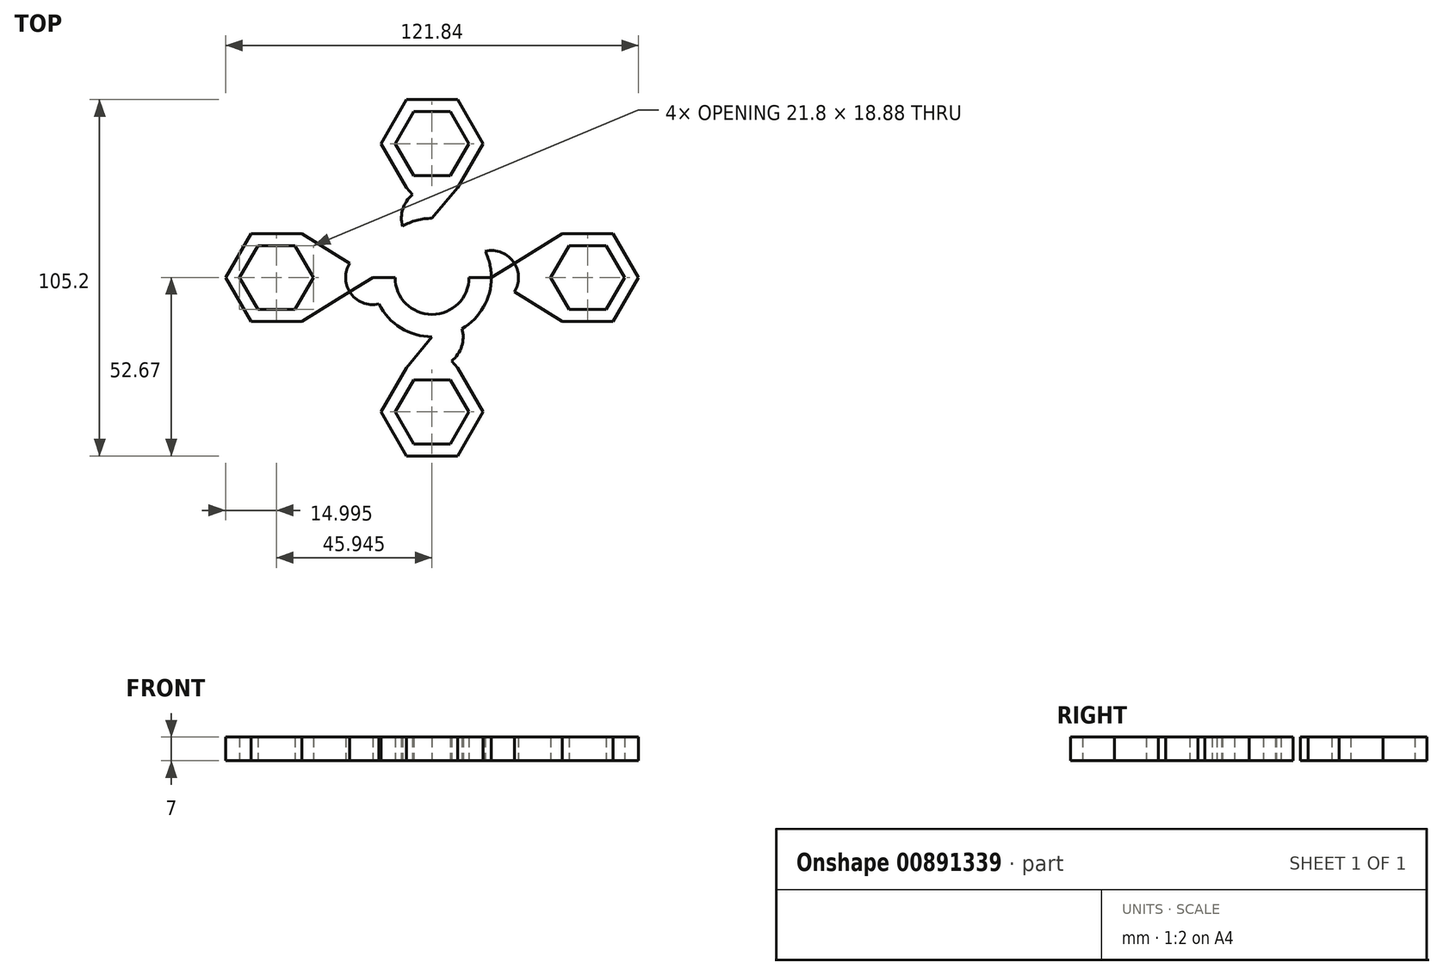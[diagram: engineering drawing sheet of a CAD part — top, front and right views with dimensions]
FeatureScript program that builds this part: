
annotation { "Feature Type Name" : "Feature", "Feature Type Description" : "" }
export const myFeature = defineFeature(function(context is Context, id is Id, definition is map)
    precondition{}
    {
        {
            var Q0;
            Q0=qCreatedBy(makeId("Top.planeOp"),FACE);
            var sketch = newSketch(context, id + "F0", { "sketchPlane" : qUnion([Q0])});
            skCircle(sketch, "E0", {"center": v(0, 0) * mm, "radius": 10.9 * mm});
            skCircle(sketch, "E1.cCircle", {"center": v(45.9, 0) * mm, "radius": 9.44 * mm, "construction": true});
            skLineSegment(sketch, "E1.0", {"start": v(40.45, 9.44) * mm, "end": v(51.35, 9.44) * mm});
            skLineSegment(sketch, "E1.1", {"start": v(51.35, 9.44) * mm, "end": v(56.8, 0) * mm});
            skLineSegment(sketch, "E1.2", {"start": v(56.8, 0) * mm, "end": v(51.35, -9.44) * mm});
            skLineSegment(sketch, "E1.3", {"start": v(51.35, -9.44) * mm, "end": v(40.45, -9.44) * mm});
            skLineSegment(sketch, "E1.4", {"start": v(40.45, -9.44) * mm, "end": v(35, 0) * mm});
            skLineSegment(sketch, "E1.5", {"start": v(35, 0) * mm, "end": v(40.45, 9.44) * mm});
            skPoint(sketch, "E1.0.midPoint", {"position": v(45.9, 9.44) * mm});
            skLineSegment(sketch, "E2", {"start": v(0, 0) * mm, "end": v(35, 0) * mm});
            skLineSegment(sketch, "E3", {"start": v(0, 0) * mm, "end": v(-35, 0) * mm});
            skCircle(sketch, "E4.cCircle", {"center": v(-45.94, 0) * mm, "radius": 9.44 * mm, "construction": true});
            skLineSegment(sketch, "E4.0", {"start": v(-51.4, 9.44) * mm, "end": v(-40.5, 9.44) * mm});
            skLineSegment(sketch, "E4.1", {"start": v(-40.5, 9.44) * mm, "end": v(-35.04, 0) * mm});
            skLineSegment(sketch, "E4.2", {"start": v(-35.04, 0) * mm, "end": v(-40.5, -9.44) * mm});
            skLineSegment(sketch, "E4.3", {"start": v(-40.5, -9.44) * mm, "end": v(-51.4, -9.44) * mm});
            skLineSegment(sketch, "E4.4", {"start": v(-51.4, -9.44) * mm, "end": v(-56.84, 0) * mm});
            skLineSegment(sketch, "E4.5", {"start": v(-56.84, 0) * mm, "end": v(-51.4, 9.44) * mm});
            skPoint(sketch, "E4.0.midPoint", {"position": v(-45.94, 9.44) * mm});
            skLineSegment(sketch, "E5", {"start": v(0, 0) * mm, "end": v(0, 30) * mm});
            skLineSegment(sketch, "E6", {"start": v(0, 30) * mm, "end": v(0, -30) * mm});
            skCircle(sketch, "E7.cCircle", {"center": v(0, -39.68) * mm, "radius": 9.44 * mm, "construction": true});
            skLineSegment(sketch, "E7.0", {"start": v(-5.45, -30.24) * mm, "end": v(5.45, -30.24) * mm});
            skLineSegment(sketch, "E7.1", {"start": v(5.45, -30.24) * mm, "end": v(10.9, -39.68) * mm});
            skLineSegment(sketch, "E7.2", {"start": v(10.9, -39.68) * mm, "end": v(5.45, -49.12) * mm});
            skLineSegment(sketch, "E7.3", {"start": v(5.45, -49.12) * mm, "end": v(-5.45, -49.12) * mm});
            skLineSegment(sketch, "E7.4", {"start": v(-5.45, -49.12) * mm, "end": v(-10.9, -39.68) * mm});
            skLineSegment(sketch, "E7.5", {"start": v(-10.9, -39.68) * mm, "end": v(-5.45, -30.24) * mm});
            skPoint(sketch, "E7.0.midPoint", {"position": v(0, -30.24) * mm});
            skCircle(sketch, "E8.cCircle", {"center": v(0, 39.54) * mm, "radius": 9.44 * mm, "construction": true});
            skLineSegment(sketch, "E8.0", {"start": v(-5.45, 48.98) * mm, "end": v(5.45, 48.98) * mm});
            skLineSegment(sketch, "E8.1", {"start": v(5.45, 48.98) * mm, "end": v(10.9, 39.54) * mm});
            skLineSegment(sketch, "E8.2", {"start": v(10.9, 39.54) * mm, "end": v(5.45, 30.1) * mm});
            skLineSegment(sketch, "E8.3", {"start": v(5.45, 30.1) * mm, "end": v(-5.45, 30.1) * mm});
            skLineSegment(sketch, "E8.4", {"start": v(-5.45, 30.1) * mm, "end": v(-10.9, 39.54) * mm});
            skLineSegment(sketch, "E8.5", {"start": v(-10.9, 39.54) * mm, "end": v(-5.45, 48.98) * mm});
            skPoint(sketch, "E8.0.midPoint", {"position": v(0, 48.98) * mm});
            skCircle(sketch, "E9", {"center": v(0, 0) * mm, "radius": 17.5 * mm});
            skCircle(sketch, "E10.cCircle", {"center": v(-45.94, 0) * mm, "radius": 13 * mm, "construction": true});
            skLineSegment(sketch, "E10.0", {"start": v(-53.44, 13) * mm, "end": v(-38.44, 13) * mm});
            skLineSegment(sketch, "E10.1", {"start": v(-38.44, 13) * mm, "end": v(-30.94, 0) * mm});
            skLineSegment(sketch, "E10.2", {"start": v(-30.94, 0) * mm, "end": v(-38.44, -13) * mm});
            skLineSegment(sketch, "E10.3", {"start": v(-38.44, -13) * mm, "end": v(-53.44, -13) * mm});
            skLineSegment(sketch, "E10.4", {"start": v(-53.44, -13) * mm, "end": v(-60.94, 0) * mm});
            skLineSegment(sketch, "E10.5", {"start": v(-60.94, 0) * mm, "end": v(-53.44, 13) * mm});
            skPoint(sketch, "E10.0.midPoint", {"position": v(-45.94, 13) * mm});
            skCircle(sketch, "E11.cCircle", {"center": v(0, 39.54) * mm, "radius": 13 * mm, "construction": true});
            skLineSegment(sketch, "E11.0", {"start": v(-7.5, 52.53) * mm, "end": v(7.5, 52.53) * mm});
            skLineSegment(sketch, "E11.1", {"start": v(7.5, 52.53) * mm, "end": v(15, 39.54) * mm});
            skLineSegment(sketch, "E11.2", {"start": v(15, 39.54) * mm, "end": v(7.5, 26.55) * mm});
            skLineSegment(sketch, "E11.3", {"start": v(7.5, 26.55) * mm, "end": v(-7.5, 26.55) * mm});
            skLineSegment(sketch, "E11.4", {"start": v(-7.5, 26.55) * mm, "end": v(-15, 39.54) * mm});
            skLineSegment(sketch, "E11.5", {"start": v(-15, 39.54) * mm, "end": v(-7.5, 52.53) * mm});
            skPoint(sketch, "E11.0.midPoint", {"position": v(0, 52.53) * mm});
            skCircle(sketch, "E12.cCircle", {"center": v(45.9, 0) * mm, "radius": 13 * mm, "construction": true});
            skLineSegment(sketch, "E12.0", {"start": v(38.4, 13) * mm, "end": v(53.4, 13) * mm});
            skLineSegment(sketch, "E12.1", {"start": v(53.4, 13) * mm, "end": v(60.9, 0) * mm});
            skLineSegment(sketch, "E12.2", {"start": v(60.9, 0) * mm, "end": v(53.4, -13) * mm});
            skLineSegment(sketch, "E12.3", {"start": v(53.4, -13) * mm, "end": v(38.4, -13) * mm});
            skLineSegment(sketch, "E12.4", {"start": v(38.4, -13) * mm, "end": v(30.9, 0) * mm});
            skLineSegment(sketch, "E12.5", {"start": v(30.9, 0) * mm, "end": v(38.4, 13) * mm});
            skPoint(sketch, "E12.0.midPoint", {"position": v(45.9, 13) * mm});
            skCircle(sketch, "E13.cCircle", {"center": v(0, -39.68) * mm, "radius": 13 * mm, "construction": true});
            skLineSegment(sketch, "E13.0", {"start": v(-7.5, -26.69) * mm, "end": v(7.5, -26.69) * mm});
            skLineSegment(sketch, "E13.1", {"start": v(7.5, -26.69) * mm, "end": v(15, -39.68) * mm});
            skLineSegment(sketch, "E13.2", {"start": v(15, -39.68) * mm, "end": v(7.5, -52.67) * mm});
            skLineSegment(sketch, "E13.3", {"start": v(7.5, -52.67) * mm, "end": v(-7.5, -52.67) * mm});
            skLineSegment(sketch, "E13.4", {"start": v(-7.5, -52.67) * mm, "end": v(-15, -39.68) * mm});
            skLineSegment(sketch, "E13.5", {"start": v(-15, -39.68) * mm, "end": v(-7.5, -26.69) * mm});
            skPoint(sketch, "E13.0.midPoint", {"position": v(0, -26.69) * mm});
            skLineSegment(sketch, "E14", {"start": v(-7.5, 26.55) * mm, "end": v(0, 17.5) * mm});
            skLineSegment(sketch, "E15", {"start": v(0, 17.5) * mm, "end": v(7.5, 26.55) * mm});
            skLineSegment(sketch, "E16", {"start": v(-7.5, -26.69) * mm, "end": v(0, -17.5) * mm});
            skLineSegment(sketch, "E17", {"start": v(0, -17.5) * mm, "end": v(7.5, -26.69) * mm});
            skLineSegment(sketch, "E18", {"start": v(38.4, -13) * mm, "end": v(17.5, 0) * mm});
            skLineSegment(sketch, "E19", {"start": v(17.5, 0) * mm, "end": v(38.4, 13) * mm});
            skLineSegment(sketch, "E20", {"start": v(-17.5, 0) * mm, "end": v(-38.44, -13) * mm});
            skLineSegment(sketch, "E21", {"start": v(-17.5, 0) * mm, "end": v(-38.44, 13) * mm});
            skLineSegment(sketch, "E22", {"start": v(-17.5, 0) * mm, "end": v(-22.5, 0) * mm});
            skLineSegment(sketch, "E23", {"start": v(17.5, 0) * mm, "end": v(22.5, 0) * mm});
            skArc(sketch, "E24", {"start": v(0, -26.69) * mm, "mid": v(7.3, -23.08) * mm, "end": v(8.86, -15.09) * mm});
            skArc(sketch, "E25", {"start": v(0, -26.69) * mm, "mid": v(-7.3, -23.08) * mm, "end": v(-8.86, -15.09) * mm});
            skArc(sketch, "E26", {"start": v(0, 26.55) * mm, "mid": v(7.18, 23) * mm, "end": v(8.74, 15.16) * mm});
            skArc(sketch, "E27", {"start": v(0, 26.55) * mm, "mid": v(-7.18, 23) * mm, "end": v(-8.74, 15.16) * mm});
            skPoint(sketch, "E28", {"position": v(27.95, -6.5) * mm});
            skPoint(sketch, "E29", {"position": v(27.95, 6.5) * mm});
            skLineSegment(sketch, "E30", {"start": v(17.5, 0) * mm, "end": v(25.5, 0) * mm});
            skLineSegment(sketch, "E31", {"start": v(-17.5, 0) * mm, "end": v(-25.5, 0) * mm});
            skArc(sketch, "E32", {"start": v(25.5, 0) * mm, "mid": v(22.47, -6.27) * mm, "end": v(15.67, -7.79) * mm});
            skArc(sketch, "E33", {"start": v(25.5, 0) * mm, "mid": v(22.47, 6.27) * mm, "end": v(15.67, 7.79) * mm});
            skArc(sketch, "E34", {"start": v(-25.5, 0) * mm, "mid": v(-22.47, -6.27) * mm, "end": v(-15.67, -7.79) * mm});
            skArc(sketch, "E35", {"start": v(-25.5, 0) * mm, "mid": v(-22.47, 6.27) * mm, "end": v(-15.67, 7.79) * mm});
            skSolve(sketch);
        }
        {
            var Q0;
            Q0=makeQuery(id+"F0.imprint","IMPRINT",FACE,{"disambiguationData":[TD([[makeQuery(id+"F0.imprint","IMPRINT",EDGE,{"derivedFrom":sQuery(id+"F0.wireOp",EDGE,"E4.0")}),1.0]])]});
            var Q1;
            {var subQ0=sQuery(id+"F0.wireOp",EDGE,"E6");var subQ1=sQuery(id+"F0.wireOp",EDGE,"E0");var subQ2=makeQuery(id+"F0.imprint","INTERSECT",VERTEX,{"disambiguationData":[OD(0.0)],"derivedFrom":[subQ1,subQ0]});Q1=makeQuery(id+"F0.imprint","IMPRINT",FACE,{"disambiguationData":[TD([[makeQuery(id+"F0.imprint","IMPRINT",EDGE,{"disambiguationData":[TD([[subQ2,1.0]])],"derivedFrom":subQ1}),-1.0]])]});}
            var Q2;
            {var subQ0=sQuery(id+"F0.wireOp",EDGE,"E2");var subQ1=sQuery(id+"F0.wireOp",EDGE,"E0");var subQ2=makeQuery(id+"F0.imprint","INTERSECT",VERTEX,{"derivedFrom":[subQ1,subQ0]});Q2=makeQuery(id+"F0.imprint","IMPRINT",FACE,{"disambiguationData":[TD([[makeQuery(id+"F0.imprint","IMPRINT",EDGE,{"disambiguationData":[TD([[subQ2,1.0]])],"derivedFrom":subQ1}),-1.0]])]});}
            var Q3;
            {var subQ0=sQuery(id+"F0.wireOp",EDGE,"E6");var subQ1=sQuery(id+"F0.wireOp",EDGE,"E0");var subQ2=makeQuery(id+"F0.imprint","INTERSECT",VERTEX,{"disambiguationData":[OD(0.0)],"derivedFrom":[subQ1,subQ0]});Q3=makeQuery(id+"F0.imprint","IMPRINT",FACE,{"disambiguationData":[TD([[makeQuery(id+"F0.imprint","IMPRINT",EDGE,{"disambiguationData":[TD([[subQ2,-1.0]])],"derivedFrom":subQ1}),-1.0]])]});}
            var Q4;
            Q4=makeQuery(id+"F0.imprint","IMPRINT",FACE,{"disambiguationData":[TD([[makeQuery(id+"F0.imprint","IMPRINT",EDGE,{"derivedFrom":sQuery(id+"F0.wireOp",EDGE,"E8.0")}),1.0]])]});
            var Q5;
            Q5=makeQuery(id+"F0.imprint","IMPRINT",FACE,{"disambiguationData":[TD([[makeQuery(id+"F0.imprint","IMPRINT",EDGE,{"derivedFrom":sQuery(id+"F0.wireOp",EDGE,"E1.0")}),1.0]])]});
            var Q6;
            Q6=makeQuery(id+"F0.imprint","IMPRINT",FACE,{"disambiguationData":[TD([[makeQuery(id+"F0.imprint","IMPRINT",EDGE,{"derivedFrom":sQuery(id+"F0.wireOp",EDGE,"E7.0")}),1.0]])]});
            var Q7;
            {var subQ0=sQuery(id+"F0.wireOp",EDGE,"E15");Q7=makeQuery(id+"F0.imprint","IMPRINT",FACE,{"disambiguationData":[TD([[makeQuery(id+"F0.imprint","IMPRINT",EDGE,{"derivedFrom":subQ0}),1.0]])]});}
            var Q8;
            {var subQ0=sQuery(id+"F0.wireOp",EDGE,"E14");Q8=makeQuery(id+"F0.imprint","IMPRINT",FACE,{"disambiguationData":[TD([[makeQuery(id+"F0.imprint","IMPRINT",EDGE,{"derivedFrom":subQ0}),1.0]])]});}
            var Q9;
            {var subQ0=sQuery(id+"F0.wireOp",EDGE,"E17");Q9=makeQuery(id+"F0.imprint","IMPRINT",FACE,{"disambiguationData":[TD([[makeQuery(id+"F0.imprint","IMPRINT",EDGE,{"derivedFrom":subQ0}),-1.0]])]});}
            var Q10;
            {var subQ0=sQuery(id+"F0.wireOp",EDGE,"E16");Q10=makeQuery(id+"F0.imprint","IMPRINT",FACE,{"disambiguationData":[TD([[makeQuery(id+"F0.imprint","IMPRINT",EDGE,{"derivedFrom":subQ0}),-1.0]])]});}
            var Q11;
            {var subQ0=sQuery(id+"F0.wireOp",EDGE,"E10.2");Q11=makeQuery(id+"F0.imprint","IMPRINT",FACE,{"disambiguationData":[TD([[makeQuery(id+"F0.imprint","IMPRINT",EDGE,{"derivedFrom":subQ0}),1.0]])]});}
            var Q12;
            {var subQ0=sQuery(id+"F0.wireOp",EDGE,"E10.1");Q12=makeQuery(id+"F0.imprint","IMPRINT",FACE,{"disambiguationData":[TD([[makeQuery(id+"F0.imprint","IMPRINT",EDGE,{"derivedFrom":subQ0}),1.0]])]});}
            var Q13;
            {var subQ0=sQuery(id+"F0.wireOp",EDGE,"E12.4");Q13=makeQuery(id+"F0.imprint","IMPRINT",FACE,{"disambiguationData":[TD([[makeQuery(id+"F0.imprint","IMPRINT",EDGE,{"derivedFrom":subQ0}),1.0]])]});}
            var Q14;
            {var subQ0=sQuery(id+"F0.wireOp",EDGE,"E12.5");Q14=makeQuery(id+"F0.imprint","IMPRINT",FACE,{"disambiguationData":[TD([[makeQuery(id+"F0.imprint","IMPRINT",EDGE,{"derivedFrom":subQ0}),1.0]])]});}
            var Q15;
            {var subQ1=sQuery(id+"F0.wireOp",EDGE,"E9");var subQ3=sQuery(id+"F0.wireOp",EDGE,"Ubq4kfX4-oC6w-lFNq-I3q3-88G8mSC7eADd");var subQ4=makeQuery(id+"F0.imprint","INTERSECT",VERTEX,{"derivedFrom":[subQ1,subQ3]});Q15=makeQuery(id+"F0.imprint","IMPRINT",FACE,{"disambiguationData":[TD([[makeQuery(id+"F0.imprint","IMPRINT",EDGE,{"disambiguationData":[TD([[subQ4,1.0]])],"derivedFrom":subQ3}),1.0]])]});}
            var Q16;
            {var subQ0=sQuery(id+"F0.wireOp",EDGE,"E22");Q16=makeQuery(id+"F0.imprint","IMPRINT",FACE,{"disambiguationData":[TD([[makeQuery(id+"F0.imprint","IMPRINT",EDGE,{"derivedFrom":subQ0}),1.0]])]});}
            var Q17;
            {var subQ1=sQuery(id+"F0.wireOp",EDGE,"E9");var subQ3=sQuery(id+"F0.wireOp",EDGE,"DwJBgmho-QLLy-2BSY-i2pv-QXPFVA0WSpVR");var subQ4=makeQuery(id+"F0.imprint","INTERSECT",VERTEX,{"derivedFrom":[subQ1,subQ3]});Q17=makeQuery(id+"F0.imprint","IMPRINT",FACE,{"disambiguationData":[TD([[makeQuery(id+"F0.imprint","IMPRINT",EDGE,{"disambiguationData":[TD([[subQ4,1.0]])],"derivedFrom":subQ3}),-1.0]])]});}
            var Q18;
            {var subQ0=sQuery(id+"F0.wireOp",EDGE,"E22");Q18=makeQuery(id+"F0.imprint","IMPRINT",FACE,{"disambiguationData":[TD([[makeQuery(id+"F0.imprint","IMPRINT",EDGE,{"derivedFrom":subQ0}),-1.0]])]});}
            var Q19;
            {var subQ1=sQuery(id+"F0.wireOp",EDGE,"E9");var subQ3=sQuery(id+"F0.wireOp",EDGE,"ud0qLV0T-u8xm-Fev3-eQ3F-uhF6uLOVjt4z");var subQ4=makeQuery(id+"F0.imprint","INTERSECT",VERTEX,{"derivedFrom":[subQ1,subQ3]});Q19=makeQuery(id+"F0.imprint","IMPRINT",FACE,{"disambiguationData":[TD([[makeQuery(id+"F0.imprint","IMPRINT",EDGE,{"disambiguationData":[TD([[subQ4,1.0]])],"derivedFrom":subQ3}),1.0]])]});}
            var Q20;
            {var subQ0=sQuery(id+"F0.wireOp",EDGE,"E23");Q20=makeQuery(id+"F0.imprint","IMPRINT",FACE,{"disambiguationData":[TD([[makeQuery(id+"F0.imprint","IMPRINT",EDGE,{"derivedFrom":subQ0}),1.0]])]});}
            var Q21;
            {var subQ0=sQuery(id+"F0.wireOp",EDGE,"E23");Q21=makeQuery(id+"F0.imprint","IMPRINT",FACE,{"disambiguationData":[TD([[makeQuery(id+"F0.imprint","IMPRINT",EDGE,{"derivedFrom":subQ0}),-1.0]])]});}
            var Q22;
            {var subQ1=sQuery(id+"F0.wireOp",EDGE,"E9");var subQ3=sQuery(id+"F0.wireOp",EDGE,"Qvp8duAn-RZq8-JCAh-Xm4F-s16nUtTtBb3N");var subQ4=makeQuery(id+"F0.imprint","INTERSECT",VERTEX,{"derivedFrom":[subQ1,subQ3]});Q22=makeQuery(id+"F0.imprint","IMPRINT",FACE,{"disambiguationData":[TD([[makeQuery(id+"F0.imprint","IMPRINT",EDGE,{"disambiguationData":[TD([[subQ4,1.0]])],"derivedFrom":subQ3}),-1.0]])]});}
            var Q23;
            {var subQ1=sQuery(id+"F0.wireOp",EDGE,"E9");var subQ3=sQuery(id+"F0.wireOp",EDGE,"c0TzAWUU-cxwK-REM3-tjBK-XptVohU1FABc");var subQ4=makeQuery(id+"F0.imprint","INTERSECT",VERTEX,{"derivedFrom":[subQ1,subQ3]});Q23=makeQuery(id+"F0.imprint","IMPRINT",FACE,{"disambiguationData":[TD([[makeQuery(id+"F0.imprint","IMPRINT",EDGE,{"disambiguationData":[TD([[subQ4,1.0]])],"derivedFrom":subQ3}),-1.0]])]});}
            var Q24;
            {var subQ1=sQuery(id+"F0.wireOp",EDGE,"E9");var subQ3=sQuery(id+"F0.wireOp",EDGE,"k8nK72Cl-iwD2-dbTf-OI5i-pcYR12xtiAX6");var subQ4=makeQuery(id+"F0.imprint","INTERSECT",VERTEX,{"derivedFrom":[subQ1,subQ3]});Q24=makeQuery(id+"F0.imprint","IMPRINT",FACE,{"disambiguationData":[TD([[makeQuery(id+"F0.imprint","IMPRINT",EDGE,{"disambiguationData":[TD([[subQ4,1.0]])],"derivedFrom":subQ3}),1.0]])]});}
            var Q25;
            {var subQ1=sQuery(id+"F0.wireOp",EDGE,"E6");var subQ3=sQuery(id+"F0.wireOp",EDGE,"E11.3");var subQ4=makeQuery(id+"F0.imprint","INTERSECT",VERTEX,{"derivedFrom":[subQ1,subQ3]});Q25=makeQuery(id+"F0.imprint","IMPRINT",FACE,{"disambiguationData":[TD([[makeQuery(id+"F0.imprint","IMPRINT",EDGE,{"disambiguationData":[TD([[subQ4,-1.0]])],"derivedFrom":subQ1}),-1.0]])]});}
            var Q26;
            {var subQ1=sQuery(id+"F0.wireOp",EDGE,"E6");var subQ3=sQuery(id+"F0.wireOp",EDGE,"E11.3");var subQ4=makeQuery(id+"F0.imprint","INTERSECT",VERTEX,{"derivedFrom":[subQ1,subQ3]});Q26=makeQuery(id+"F0.imprint","IMPRINT",FACE,{"disambiguationData":[TD([[makeQuery(id+"F0.imprint","IMPRINT",EDGE,{"disambiguationData":[TD([[subQ4,-1.0]])],"derivedFrom":subQ1}),1.0]])]});}
            var Q27;
            {var subQ1=sQuery(id+"F0.wireOp",EDGE,"E9");var subQ3=sQuery(id+"F0.wireOp",EDGE,"E25");var subQ4=makeQuery(id+"F0.imprint","INTERSECT",VERTEX,{"derivedFrom":[subQ1,subQ3]});Q27=makeQuery(id+"F0.imprint","IMPRINT",FACE,{"disambiguationData":[TD([[makeQuery(id+"F0.imprint","IMPRINT",EDGE,{"disambiguationData":[TD([[subQ4,1.0]])],"derivedFrom":subQ3}),-1.0]])]});}
            var Q28;
            {var subQ1=sQuery(id+"F0.wireOp",EDGE,"E9");var subQ3=sQuery(id+"F0.wireOp",EDGE,"E24");var subQ4=makeQuery(id+"F0.imprint","INTERSECT",VERTEX,{"derivedFrom":[subQ1,subQ3]});Q28=makeQuery(id+"F0.imprint","IMPRINT",FACE,{"disambiguationData":[TD([[makeQuery(id+"F0.imprint","IMPRINT",EDGE,{"disambiguationData":[TD([[subQ4,1.0]])],"derivedFrom":subQ3}),1.0]])]});}
            var Q29;
            {var subQ1=sQuery(id+"F0.wireOp",EDGE,"E9");var subQ3=sQuery(id+"F0.wireOp",EDGE,"E32");var subQ4=makeQuery(id+"F0.imprint","INTERSECT",VERTEX,{"derivedFrom":[subQ1,subQ3]});Q29=makeQuery(id+"F0.imprint","IMPRINT",FACE,{"disambiguationData":[TD([[makeQuery(id+"F0.imprint","IMPRINT",EDGE,{"disambiguationData":[TD([[subQ4,1.0]])],"derivedFrom":subQ3}),-1.0]])]});}
            var Q30;
            {var subQ1=sQuery(id+"F0.wireOp",EDGE,"E9");var subQ3=sQuery(id+"F0.wireOp",EDGE,"E33");var subQ4=makeQuery(id+"F0.imprint","INTERSECT",VERTEX,{"derivedFrom":[subQ1,subQ3]});Q30=makeQuery(id+"F0.imprint","IMPRINT",FACE,{"disambiguationData":[TD([[makeQuery(id+"F0.imprint","IMPRINT",EDGE,{"disambiguationData":[TD([[subQ4,1.0]])],"derivedFrom":subQ3}),1.0]])]});}
            var Q31;
            {var subQ0=sQuery(id+"F0.wireOp",EDGE,"E30");var subQ7=makeQuery(id+"F0.imprint","IMPRINT",VERTEX,{"derivedFrom":subQ0});Q31=makeQuery(id+"F0.imprint","IMPRINT",FACE,{"disambiguationData":[TD([[makeQuery(id+"F0.imprint","IMPRINT",EDGE,{"disambiguationData":[TD([[subQ7,-1.0]])],"derivedFrom":subQ0}),1.0]])]});}
            var Q32;
            {var subQ0=sQuery(id+"F0.wireOp",EDGE,"E30");var subQ6=makeQuery(id+"F0.imprint","IMPRINT",VERTEX,{"derivedFrom":subQ0});Q32=makeQuery(id+"F0.imprint","IMPRINT",FACE,{"disambiguationData":[TD([[makeQuery(id+"F0.imprint","IMPRINT",EDGE,{"disambiguationData":[TD([[subQ6,-1.0]])],"derivedFrom":subQ0}),-1.0]])]});}
            var Q33;
            {var subQ1=sQuery(id+"F0.wireOp",EDGE,"E9");var subQ3=sQuery(id+"F0.wireOp",EDGE,"E34");var subQ4=makeQuery(id+"F0.imprint","INTERSECT",VERTEX,{"derivedFrom":[subQ1,subQ3]});Q33=makeQuery(id+"F0.imprint","IMPRINT",FACE,{"disambiguationData":[TD([[makeQuery(id+"F0.imprint","IMPRINT",EDGE,{"disambiguationData":[TD([[subQ4,1.0]])],"derivedFrom":subQ3}),1.0]])]});}
            var Q34;
            {var subQ1=sQuery(id+"F0.wireOp",EDGE,"E3");var subQ4=sQuery(id+"F0.wireOp",EDGE,"E0");var subQ5=makeQuery(id+"F0.imprint","INTERSECT",VERTEX,{"derivedFrom":[subQ4,subQ1]});Q34=makeQuery(id+"F0.imprint","IMPRINT",FACE,{"disambiguationData":[TD([[makeQuery(id+"F0.imprint","IMPRINT",EDGE,{"disambiguationData":[TD([[subQ5,-1.0]])],"derivedFrom":subQ4}),-1.0]])]});}
            var Q35;
            {var subQ0=sQuery(id+"F0.wireOp",EDGE,"E31");var subQ7=makeQuery(id+"F0.imprint","IMPRINT",VERTEX,{"derivedFrom":subQ0});Q35=makeQuery(id+"F0.imprint","IMPRINT",FACE,{"disambiguationData":[TD([[makeQuery(id+"F0.imprint","IMPRINT",EDGE,{"disambiguationData":[TD([[subQ7,-1.0]])],"derivedFrom":subQ0}),1.0]])]});}
            var Q36;
            {var subQ0=sQuery(id+"F0.wireOp",EDGE,"E31");var subQ7=makeQuery(id+"F0.imprint","IMPRINT",VERTEX,{"derivedFrom":subQ0});Q36=makeQuery(id+"F0.imprint","IMPRINT",FACE,{"disambiguationData":[TD([[makeQuery(id+"F0.imprint","IMPRINT",EDGE,{"disambiguationData":[TD([[subQ7,-1.0]])],"derivedFrom":subQ0}),-1.0]])]});}
            var Q37;
            {var subQ1=sQuery(id+"F0.wireOp",EDGE,"E9");var subQ3=sQuery(id+"F0.wireOp",EDGE,"E35");var subQ4=makeQuery(id+"F0.imprint","INTERSECT",VERTEX,{"derivedFrom":[subQ1,subQ3]});Q37=makeQuery(id+"F0.imprint","IMPRINT",FACE,{"disambiguationData":[TD([[makeQuery(id+"F0.imprint","IMPRINT",EDGE,{"disambiguationData":[TD([[subQ4,1.0]])],"derivedFrom":subQ3}),-1.0]])]});}
            var Q38;
            {var subQ1=sQuery(id+"F0.wireOp",EDGE,"E9");var subQ3=sQuery(id+"F0.wireOp",EDGE,"E27");var subQ4=makeQuery(id+"F0.imprint","INTERSECT",VERTEX,{"derivedFrom":[subQ1,subQ3]});Q38=makeQuery(id+"F0.imprint","IMPRINT",FACE,{"disambiguationData":[TD([[makeQuery(id+"F0.imprint","IMPRINT",EDGE,{"disambiguationData":[TD([[subQ4,1.0]])],"derivedFrom":subQ3}),1.0]])]});}
            var Q39;
            {var subQ1=sQuery(id+"F0.wireOp",EDGE,"E9");var subQ3=sQuery(id+"F0.wireOp",EDGE,"E26");var subQ4=makeQuery(id+"F0.imprint","INTERSECT",VERTEX,{"derivedFrom":[subQ1,subQ3]});Q39=makeQuery(id+"F0.imprint","IMPRINT",FACE,{"disambiguationData":[TD([[makeQuery(id+"F0.imprint","IMPRINT",EDGE,{"disambiguationData":[TD([[subQ4,1.0]])],"derivedFrom":subQ3}),-1.0]])]});}
            extrude(context, id + "F1", {"entities" : qUnion([Q0, Q1, Q2, Q3, Q4, Q5, Q6, Q7, Q8, Q9, Q10, Q11, Q12, Q13, Q14, Q15, Q16, Q17, Q18, Q19, Q20, Q21, Q22, Q23, Q24, Q25, Q26, Q27, Q28, Q29, Q30, Q31, Q32, Q33, Q34, Q35, Q36, Q37, Q38, Q39]), "depth" : 7 * mm, "offsetDistance" : 25 * mm});
        }
    });
